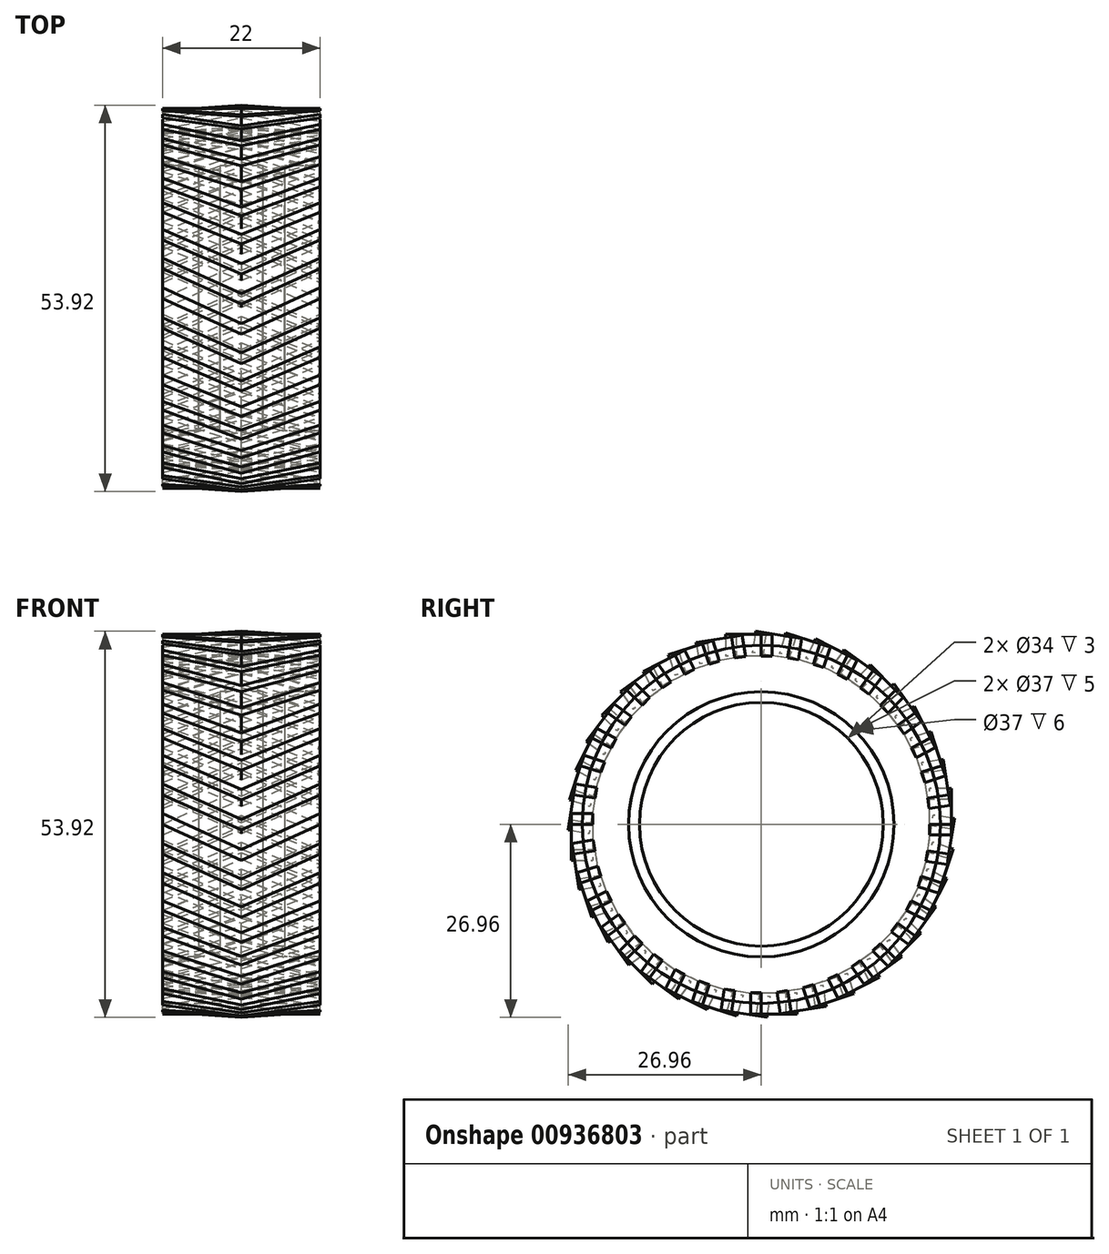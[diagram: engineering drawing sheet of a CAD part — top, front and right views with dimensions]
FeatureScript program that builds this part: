
annotation { "Feature Type Name" : "Feature", "Feature Type Description" : "" }
export const myFeature = defineFeature(function(context is Context, id is Id, definition is map)
    precondition{}
    {
        {
            var Q0;
            Q0=qCreatedBy(makeId("Front.planeOp"),FACE);
            var sketch = newSketch(context, id + "F0", { "sketchPlane" : qUnion([Q0])});
            skLineSegment(sketch, "E0", {"start": v(0, 18.5) * mm, "end": v(-3, 18.5) * mm});
            skLineSegment(sketch, "E1", {"start": v(-3, 18.5) * mm, "end": v(-3, 17) * mm});
            skLineSegment(sketch, "E2", {"start": v(-3, 17) * mm, "end": v(-6, 17) * mm});
            skLineSegment(sketch, "E3", {"start": v(-6, 17) * mm, "end": v(-6, 18.5) * mm});
            skLineSegment(sketch, "E4", {"start": v(-6, 18.5) * mm, "end": v(-11, 18.5) * mm});
            skLineSegment(sketch, "E5", {"start": v(-11, 18.5) * mm, "end": v(-11, 25) * mm});
            skLineSegment(sketch, "E6.MirrorCS", {"start": v(3, 18.5) * mm, "end": v(3, 17) * mm});
            skLineSegment(sketch, "E7.MirrorCS", {"start": v(6, 17) * mm, "end": v(6, 18.5) * mm});
            skLineSegment(sketch, "E8.MirrorCS", {"start": v(0, 18.5) * mm, "end": v(3, 18.5) * mm});
            skLineSegment(sketch, "E9.MirrorCS", {"start": v(11, 18.5) * mm, "end": v(11, 25) * mm});
            skLineSegment(sketch, "E10.MirrorCS", {"start": v(6, 18.5) * mm, "end": v(11, 18.5) * mm});
            skLineSegment(sketch, "E11.MirrorCS", {"start": v(3, 17) * mm, "end": v(6, 17) * mm});
            skLineSegment(sketch, "E12", {"start": v(-11, 0) * mm, "end": v(11, 0) * mm});
            skLineSegment(sketch, "E13", {"start": v(-11, 25) * mm, "end": v(11, 25) * mm});
            skSolve(sketch);
        }
        {
            var Q0;
            Q0=makeQuery(id+"F0.imprint","IMPRINT",FACE,{"disambiguationData":[TD([[makeQuery(id+"F0.imprint","IMPRINT",EDGE,{"derivedFrom":sQuery(id+"F0.wireOp",EDGE,"E0")}),-1.0]])]});
            var Q1;
            Q1=sQuery(id+"F0.wireOp",EDGE,"E12");
            revolve(context, id + "F1", {"surfaceOperationType" : NewSurfaceOperationType.NEW, "entities" : qUnion([Q0]), "axis" : qUnion([Q1]), "revolveType" : RevolveType.FULL});
        }
        {
            var Q0;
            Q0=qCreatedBy(makeId("Top.planeOp"),FACE);
            var sketch = newSketch(context, id + "F2", { "sketchPlane" : qUnion([Q0])});
            skLineSegment(sketch, "E14", {"start": v(-11, 0) * mm, "end": v(0, -5) * mm});
            skLineSegment(sketch, "E15", {"start": v(0, -5) * mm, "end": v(11, 0) * mm});
            skLineSegment(sketch, "E16", {"start": v(0, -5) * mm, "end": v(0, -3.5) * mm, "construction": true});
            skLineSegment(sketch, "E17", {"start": v(-11, 1.5) * mm, "end": v(0, -3.5) * mm});
            skLineSegment(sketch, "E18", {"start": v(0, -3.5) * mm, "end": v(11, 1.5) * mm});
            skLineSegment(sketch, "E19", {"start": v(-11, 1.5) * mm, "end": v(-11, 0) * mm});
            skLineSegment(sketch, "E20", {"start": v(11, 1.5) * mm, "end": v(11, 0) * mm});
            skSolve(sketch);
        }
        {
            var Q0;
            Q0=makeQuery(id+"F2.imprint","IMPRINT",FACE,{"disambiguationData":[TD([[makeQuery(id+"F2.imprint","IMPRINT",EDGE,{"derivedFrom":sQuery(id+"F2.wireOp",EDGE,"E14")}),1.0]])]});
            extrude(context, id + "F3", {"entities" : qUnion([Q0]), "depth" : 26.5 * mm, "offsetDistance" : 25 * mm, "hasSecondDirection" : true, "secondDirectionOppositeDirection" : false, "secondDirectionDepth" : 23.5 * mm});
        }
        {
            var Q0;
            Q0=makeQuery(id+"F3.opExtrude","SWEPT_BODY",BODY,{"disambiguationData":[OSD([sQuery(id+"F2.wireOp",EDGE,"E14"),sQuery(id+"F2.wireOp",EDGE,"E15"),sQuery(id+"F2.wireOp",EDGE,"E17"),sQuery(id+"F2.wireOp",EDGE,"E18"),sQuery(id+"F2.wireOp",EDGE,"E19"),sQuery(id+"F2.wireOp",EDGE,"E20")])]});
            var Q1;
            Q1=sQuery(id+"F0.wireOp",EDGE,"E12");
            circularPattern(context, id + "F4", {"entities" : qUnion([Q0]), "axis" : qUnion([Q1]), "angle" : 360 * degree, "instanceCount" : 40, "equalSpace" : true});
        }
    });
